# Revit family: Wall_Mount-Tempo-Chief-FPIWMS--
name_source: partatom
category: Specialty Equipment
units: mm (PartAtom-declared; Revit-internal decimal feet)

## family parameters
Cut with Voids When Loaded = Yes
Host = Face
OmniClass Number = 23.85.10.17.11
OmniClass Title = Audio-Visual System Components
Part Type = Normal
Room Calculation Point = No
Round Connector Dimension = Use Diameter
Shared = No

## types (2) — shared parameters
Assembly Code = E2010
Date Modified = May 24, 2024
Default Elevation = 48 "
Description = See Part Description
ENGworks Global = https://engworksglobal.com
Electrical Box Material = Aluminum
Family Version = 2.0
Finish = Metal - Legrand - Black Finish
Inner Height = 23 "
Inner Width = 13.81 "
Manufacturer = Chief
Model = See Part Number
Model Disclaimer = Contact Chief For More Information
Part Number = FPIWMS
Product Page URL = https://www.legrandav.com
URL = https://www.legrandav.com

## per-type parameters (varying)
| type | Separate | Together |
| FPIWMS Together | No | Yes |
| FPIWMS Separate | Yes | No |

## geometry (parser evidence)
native form markers: Sweep x19
no freeform markers — native parametric forms only
